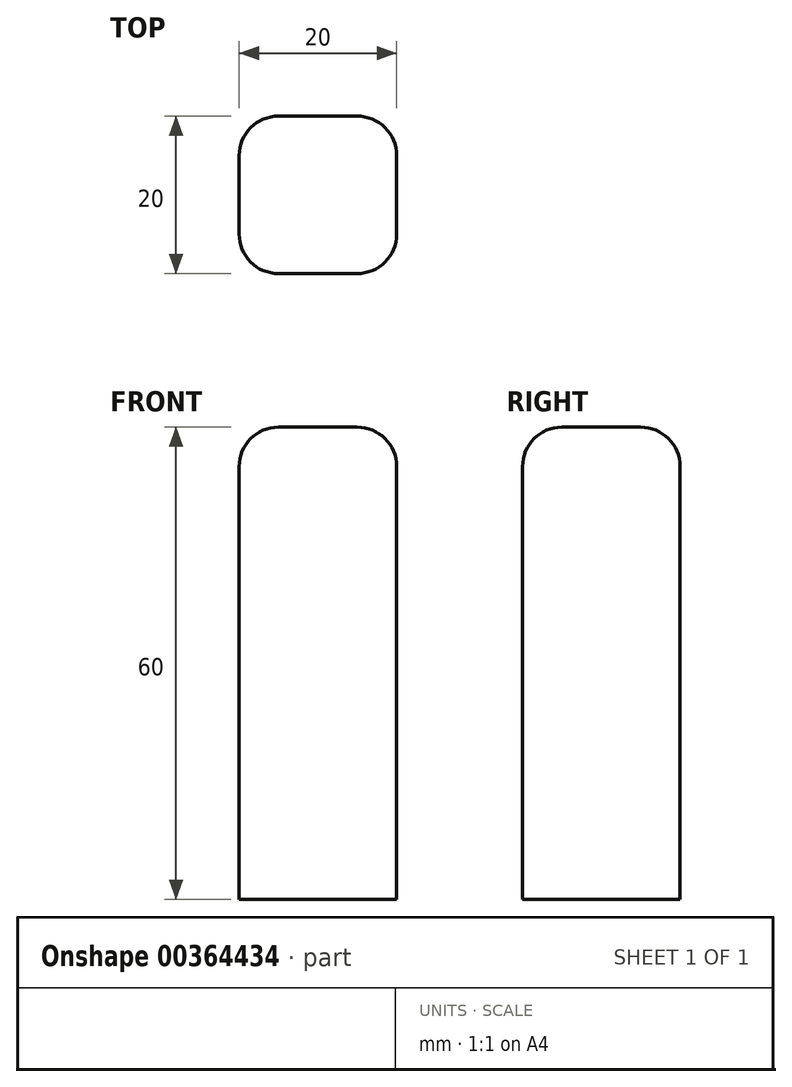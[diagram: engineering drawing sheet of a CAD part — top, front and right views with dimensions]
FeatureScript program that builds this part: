
annotation { "Feature Type Name" : "Feature", "Feature Type Description" : "" }
export const myFeature = defineFeature(function(context is Context, id is Id, definition is map)
    precondition{}
    {
        {
            var Q0;
            Q0=qCreatedBy(makeId("Top.planeOp"),FACE);
            var sketch = newSketch(context, id + "F0", { "sketchPlane" : qUnion([Q0])});
            skLineSegment(sketch, "E0.bottom", {"start": v(10, -10) * mm, "end": v(-10, -10) * mm});
            skLineSegment(sketch, "E0.top", {"start": v(10, 10) * mm, "end": v(-10, 10) * mm});
            skLineSegment(sketch, "E0.left", {"start": v(10, -10) * mm, "end": v(10, 10) * mm});
            skLineSegment(sketch, "E0.right", {"start": v(-10, -10) * mm, "end": v(-10, 10) * mm});
            skPoint(sketch, "E0.middle", {"position": v(0, 0) * mm});
            skSolve(sketch);
        }
        {
            var Q0;
            Q0 = qSketchRegion(id + "F0", true);
            extrude(context, id + "F1", {"entities" : qUnion([Q0]), "depth" : 60 * mm});
        }
        {
            var Q0;
            Q0=makeQuery(id+"F1.opExtrude","CAP_FACE",FACE,{"disambiguationData":[OSD([sQuery(id+"F0.wireOp",EDGE,"E0.bottom"),sQuery(id+"F0.wireOp",EDGE,"E0.top"),sQuery(id+"F0.wireOp",EDGE,"E0.left"),sQuery(id+"F0.wireOp",EDGE,"E0.right")])],"isStart":false});
            var Q1;
            Q1=makeQuery(id+"F1.opExtrude","SWEPT_EDGE",EDGE,{"disambiguationData":[OSD([sQuery(id+"F0.wireOp",EDGE,"E0.bottom"),sQuery(id+"F0.wireOp",EDGE,"E0.left")])]});
            var Q2;
            Q2=makeQuery(id+"F1.opExtrude","SWEPT_EDGE",EDGE,{"disambiguationData":[OSD([sQuery(id+"F0.wireOp",EDGE,"E0.top"),sQuery(id+"F0.wireOp",EDGE,"E0.left")])]});
            var Q3;
            Q3=makeQuery(id+"F1.opExtrude","SWEPT_EDGE",EDGE,{"disambiguationData":[OSD([sQuery(id+"F0.wireOp",EDGE,"E0.bottom"),sQuery(id+"F0.wireOp",EDGE,"E0.right")])]});
            var Q4;
            Q4=makeQuery(id+"F1.opExtrude","SWEPT_EDGE",EDGE,{"disambiguationData":[OSD([sQuery(id+"F0.wireOp",EDGE,"E0.top"),sQuery(id+"F0.wireOp",EDGE,"E0.right")])]});
            fillet(context, id + "F2", {"entities" : qUnion([Q0, Q1, Q2, Q3, Q4]), "radius" : 5 * mm, "tangentPropagation" : true, "allowEdgeOverflow" : false});
        }
    });
